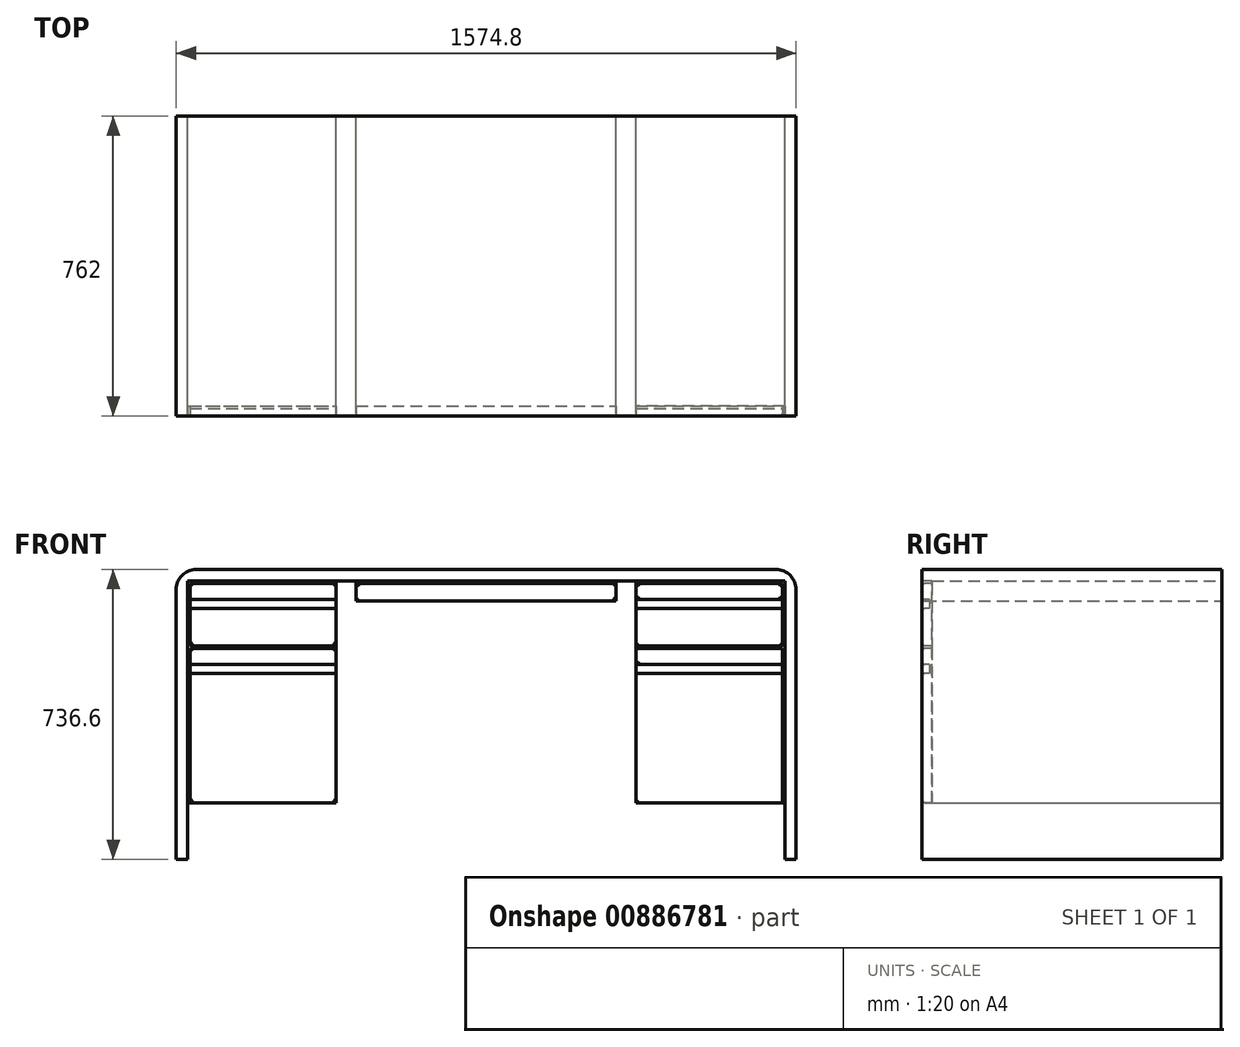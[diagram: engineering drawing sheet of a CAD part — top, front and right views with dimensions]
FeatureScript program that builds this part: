
annotation { "Feature Type Name" : "Feature", "Feature Type Description" : "" }
export const myFeature = defineFeature(function(context is Context, id is Id, definition is map)
    precondition{}
    {
        {
            var Q0;
            Q0=qCreatedBy(makeId("Front.planeOp"),FACE);
            var sketch = newSketch(context, id + "F0", { "sketchPlane" : qUnion([Q0])});
            skLineSegment(sketch, "E0.bottom", {"start": v(-787.4, 368.3) * mm, "end": v(787.4, 368.3) * mm});
            skLineSegment(sketch, "E0.top", {"start": v(-787.4, -368.3) * mm, "end": v(-758.83, -368.3) * mm});
            skLineSegment(sketch, "E0.left", {"start": v(-787.4, 368.3) * mm, "end": v(-787.4, -368.3) * mm});
            skLineSegment(sketch, "E0.right", {"start": v(787.4, 368.3) * mm, "end": v(787.4, -368.3) * mm});
            skPoint(sketch, "E0.middle", {"position": v(0, 0) * mm});
            skLineSegment(sketch, "E1", {"start": v(-758.83, -368.3) * mm, "end": v(-758.83, -224.1) * mm});
            skLineSegment(sketch, "E2", {"start": v(-758.83, -224.1) * mm, "end": v(-381, -224.1) * mm});
            skLineSegment(sketch, "E3", {"start": v(-381, -224.1) * mm, "end": v(-381, 339.73) * mm});
            skLineSegment(sketch, "E4", {"start": v(-381, 339.73) * mm, "end": v(-330.2, 339.73) * mm});
            skLineSegment(sketch, "E5", {"start": v(-330.2, 339.72) * mm, "end": v(-330.2, 288.93) * mm});
            skLineSegment(sketch, "E6", {"start": v(-330.2, 288.93) * mm, "end": v(330.2, 288.93) * mm});
            skLineSegment(sketch, "E7", {"start": v(330.2, 288.93) * mm, "end": v(330.2, 339.73) * mm});
            skLineSegment(sketch, "E8", {"start": v(330.2, 339.73) * mm, "end": v(381, 339.73) * mm});
            skLineSegment(sketch, "E9", {"start": v(381, 339.73) * mm, "end": v(381, -224.1) * mm});
            skLineSegment(sketch, "E10", {"start": v(381, -224.1) * mm, "end": v(758.83, -224.1) * mm});
            skLineSegment(sketch, "E11", {"start": v(758.83, -224.1) * mm, "end": v(758.83, -368.3) * mm});
            skLineSegment(sketch, "E12.trimOffspring", {"start": v(758.83, -368.3) * mm, "end": v(787.4, -368.3) * mm});
            skSolve(sketch);
        }
        {
            var Q0;
            Q0=makeQuery(id+"F0.imprint","IMPRINT",FACE,{"disambiguationData":[TD([[makeQuery(id+"F0.imprint","IMPRINT",EDGE,{"derivedFrom":sQuery(id+"F0.wireOp",EDGE,"E0.bottom")}),-1.0]])]});
            extrude(context, id + "F1", {"entities" : qUnion([Q0]), "endBound" : BoundingType.SYMMETRIC, "depth" : 762 * mm, "offsetDistance" : 25.4 * mm});
        }
        {
            var Q0;
            Q0=makeQuery(id+"F1.opExtrude","SWEPT_EDGE",EDGE,{"disambiguationData":[OSD([sQuery(id+"F0.wireOp",EDGE,"E0.bottom"),sQuery(id+"F0.wireOp",EDGE,"E0.right")])]});
            var Q1;
            Q1=makeQuery(id+"F1.opExtrude","SWEPT_EDGE",EDGE,{"disambiguationData":[OSD([sQuery(id+"F0.wireOp",EDGE,"E0.bottom"),sQuery(id+"F0.wireOp",EDGE,"E0.left")])]});
            fillet(context, id + "F2", {"entities" : qUnion([Q0, Q1]), "radius" : 50.8 * mm, "tangentPropagation" : true, "allowEdgeOverflow" : false});
        }
        {
            var Q0;
            Q0=makeQuery(id+"F1.opExtrude","CAP_FACE",FACE,{"disambiguationData":[OSD([sQuery(id+"F0.wireOp",EDGE,"E0.bottom"),sQuery(id+"F0.wireOp",EDGE,"E0.top"),sQuery(id+"F0.wireOp",EDGE,"E0.left"),sQuery(id+"F0.wireOp",EDGE,"E0.right"),sQuery(id+"F0.wireOp",EDGE,"E1"),sQuery(id+"F0.wireOp",EDGE,"E2"),sQuery(id+"F0.wireOp",EDGE,"E3"),sQuery(id+"F0.wireOp",EDGE,"E4"),sQuery(id+"F0.wireOp",EDGE,"E5"),sQuery(id+"F0.wireOp",EDGE,"E6"),sQuery(id+"F0.wireOp",EDGE,"E7"),sQuery(id+"F0.wireOp",EDGE,"E8"),sQuery(id+"F0.wireOp",EDGE,"E9"),sQuery(id+"F0.wireOp",EDGE,"E10"),sQuery(id+"F0.wireOp",EDGE,"E11"),sQuery(id+"F0.wireOp",EDGE,"E12.trimOffspring")])],"isStart":false});
            var sketch = newSketch(context, id + "F3", { "sketchPlane" : qUnion([Q0])});
            skLineSegment(sketch, "E13", {"start": v(-758.83, -224.1) * mm, "end": v(-758.83, 339.73) * mm});
            skLineSegment(sketch, "E14", {"start": v(-758.83, 339.73) * mm, "end": v(-381, 339.73) * mm});
            skLineSegment(sketch, "E15", {"start": v(-752.48, -224.1) * mm, "end": v(-752.48, 168.28) * mm});
            skLineSegment(sketch, "E16", {"start": v(-752.48, 333.38) * mm, "end": v(-381, 333.38) * mm});
            skLineSegment(sketch, "E17", {"start": v(-752.48, 174.63) * mm, "end": v(-381, 174.63) * mm});
            skLineSegment(sketch, "E18", {"start": v(-752.48, 168.28) * mm, "end": v(-381, 168.28) * mm});
            skLineSegment(sketch, "E19.trimOffspring", {"start": v(-752.48, 174.63) * mm, "end": v(-752.48, 333.38) * mm});
            skLineSegment(sketch, "E20", {"start": v(-330.2, 339.73) * mm, "end": v(330.2, 339.73) * mm});
            skLineSegment(sketch, "E21", {"start": v(-330.2, 333.38) * mm, "end": v(330.2, 333.38) * mm});
            skLineSegment(sketch, "E22", {"start": v(758.83, -224.1) * mm, "end": v(758.83, 339.73) * mm});
            skLineSegment(sketch, "E23", {"start": v(758.83, 339.73) * mm, "end": v(381, 339.73) * mm});
            skLineSegment(sketch, "E24", {"start": v(381, 333.38) * mm, "end": v(752.48, 333.38) * mm});
            skLineSegment(sketch, "E25", {"start": v(752.48, 333.38) * mm, "end": v(752.48, 174.63) * mm});
            skLineSegment(sketch, "E26", {"start": v(381, 174.63) * mm, "end": v(752.48, 174.63) * mm});
            skLineSegment(sketch, "E27", {"start": v(381, 168.28) * mm, "end": v(752.48, 168.28) * mm});
            skLineSegment(sketch, "E28.trimOffspring", {"start": v(752.48, 168.28) * mm, "end": v(752.48, -224.1) * mm});
            skLineSegment(sketch, "E29", {"start": v(-752.48, 292.1) * mm, "end": v(-381, 292.1) * mm});
            skLineSegment(sketch, "E30", {"start": v(-752.48, 269.87) * mm, "end": v(-381, 269.87) * mm});
            skLineSegment(sketch, "E31", {"start": v(-752.48, 127) * mm, "end": v(-381, 127) * mm});
            skLineSegment(sketch, "E32", {"start": v(-752.48, 104.77) * mm, "end": v(-381, 104.77) * mm});
            skLineSegment(sketch, "E33", {"start": v(381, 292.1) * mm, "end": v(752.48, 292.1) * mm});
            skLineSegment(sketch, "E34", {"start": v(381, 269.87) * mm, "end": v(752.48, 269.87) * mm});
            skLineSegment(sketch, "E35", {"start": v(381, 127) * mm, "end": v(752.48, 127) * mm});
            skLineSegment(sketch, "E36", {"start": v(381, 104.77) * mm, "end": v(752.48, 104.77) * mm});
            skSolve(sketch);
        }
        {
            var Q0;
            {var subQ8=sQuery(id+"F3.wireOp",EDGE,"E13");Q0=makeQuery(id+"F3.imprint","IMPRINT",FACE,{"disambiguationData":[TD([[makeQuery(id+"F3.imprint","IMPRINT",EDGE,{"derivedFrom":subQ8}),-1.0]])]});}
            var Q1;
            {var subQ0=sQuery(id+"F3.wireOp",EDGE,"E20");Q1=makeQuery(id+"F3.imprint","IMPRINT",FACE,{"disambiguationData":[TD([[makeQuery(id+"F3.imprint","IMPRINT",EDGE,{"derivedFrom":subQ0}),-1.0]])]});}
            var Q2;
            {var subQ4=sQuery(id+"F3.wireOp",EDGE,"E22");Q2=makeQuery(id+"F3.imprint","IMPRINT",FACE,{"disambiguationData":[TD([[makeQuery(id+"F3.imprint","IMPRINT",EDGE,{"derivedFrom":subQ4}),1.0]])]});}
            extrude(context, id + "F4", {"entities" : qUnion([Q0, Q1, Q2]), "operationType" : NewBodyOperationType.REMOVE, "oppositeDirection" : true, "depth" : 25.4 * mm, "offsetDistance" : 25.4 * mm});
        }
        {
            var Q0;
            {var subQ0=sQuery(id+"F3.wireOp",EDGE,"E31");Q0=makeQuery(id+"F3.imprint","IMPRINT",FACE,{"disambiguationData":[TD([[makeQuery(id+"F3.imprint","IMPRINT",EDGE,{"derivedFrom":subQ0}),-1.0]])]});}
            var Q1;
            {var subQ0=sQuery(id+"F3.wireOp",EDGE,"E29");Q1=makeQuery(id+"F3.imprint","IMPRINT",FACE,{"disambiguationData":[TD([[makeQuery(id+"F3.imprint","IMPRINT",EDGE,{"derivedFrom":subQ0}),-1.0]])]});}
            var Q2;
            {var subQ0=sQuery(id+"F3.wireOp",EDGE,"E33");Q2=makeQuery(id+"F3.imprint","IMPRINT",FACE,{"disambiguationData":[TD([[makeQuery(id+"F3.imprint","IMPRINT",EDGE,{"derivedFrom":subQ0}),-1.0]])]});}
            var Q3;
            {var subQ0=sQuery(id+"F3.wireOp",EDGE,"E35");Q3=makeQuery(id+"F3.imprint","IMPRINT",FACE,{"disambiguationData":[TD([[makeQuery(id+"F3.imprint","IMPRINT",EDGE,{"derivedFrom":subQ0}),-1.0]])]});}
            extrude(context, id + "F5", {"entities" : qUnion([Q0, Q1, Q2, Q3]), "operationType" : NewBodyOperationType.REMOVE, "oppositeDirection" : true, "depth" : 19.05 * mm, "offsetDistance" : 25.4 * mm});
        }
        {
            var Q0;
            Q0=makeQuery(id+"F1.opExtrude","CAP_EDGE",EDGE,{"disambiguationData":[OSD([sQuery(id+"F0.wireOp",EDGE,"E2")])],"isStart":false});
            var Q1;
            {var subQ0=sQuery(id+"F0.wireOp",EDGE,"E3");var subQ1=sQuery(id+"F0.wireOp",EDGE,"E2");var subQ3=makeQuery(id+"F1.opExtrude","SWEPT_FACE",FACE,{"disambiguationData":[OSD([subQ1])]});Q1=makeQuery(id+"F5.boolean.opBoolean","SPLIT",EDGE,{"disambiguationData":[TD([subQ3])],"derivedFrom":makeQuery(id+"F4.boolean.opBoolean","SPLIT",EDGE,{"disambiguationData":[TD([subQ3])],"derivedFrom":makeQuery(id+"F1.opExtrude","CAP_EDGE",EDGE,{"disambiguationData":[OSD([subQ0])],"isStart":false})})});}
            var Q2;
            {var subQ0=sQuery(id+"F0.wireOp",EDGE,"E3");var subQ1=sQuery(id+"F0.wireOp",EDGE,"E2");var subQ3=makeQuery(id+"F4.opExtrude","SWEPT_FACE",FACE,{"disambiguationData":[OSD([sQuery(id+"F3.wireOp",EDGE,"E18")])]});Q2=makeQuery(id+"F5.boolean.opBoolean","SPLIT",EDGE,{"disambiguationData":[TD([makeQuery(id+"F4.boolean.opBoolean","COPY",FACE,{"derivedFrom":subQ3})])],"derivedFrom":makeQuery(id+"F4.boolean.opBoolean","SPLIT",EDGE,{"disambiguationData":[TD([makeQuery(id+"F1.opExtrude","SWEPT_FACE",FACE,{"disambiguationData":[OSD([subQ1])]})])],"derivedFrom":makeQuery(id+"F1.opExtrude","CAP_EDGE",EDGE,{"disambiguationData":[OSD([subQ0])],"isStart":false})})});}
            var Q3;
            {var subQ0=sQuery(id+"F0.wireOp",EDGE,"E3");var subQ3=makeQuery(id+"F4.opExtrude","SWEPT_FACE",FACE,{"disambiguationData":[OSD([sQuery(id+"F3.wireOp",EDGE,"E17")])]});Q3=makeQuery(id+"F5.boolean.opBoolean","SPLIT",EDGE,{"disambiguationData":[TD([makeQuery(id+"F4.boolean.opBoolean","COPY",FACE,{"derivedFrom":subQ3})])],"derivedFrom":makeQuery(id+"F4.boolean.opBoolean","SPLIT",EDGE,{"disambiguationData":[TD([makeQuery(id+"F4.opExtrude","SWEPT_FACE",FACE,{"disambiguationData":[OSD([sQuery(id+"F3.wireOp",EDGE,"E16")])]})])],"derivedFrom":makeQuery(id+"F1.opExtrude","CAP_EDGE",EDGE,{"disambiguationData":[OSD([subQ0])],"isStart":false})})});}
            var Q4;
            Q4=makeQuery(id+"F4.boolean.opBoolean","COPY",EDGE,{"derivedFrom":makeQuery(id+"F4.opExtrude","CAP_EDGE",EDGE,{"disambiguationData":[OSD([sQuery(id+"F3.wireOp",EDGE,"E18")])],"isStart":true})});
            var Q5;
            Q5=makeQuery(id+"F4.boolean.opBoolean","COPY",EDGE,{"derivedFrom":makeQuery(id+"F4.opExtrude","CAP_EDGE",EDGE,{"disambiguationData":[OSD([sQuery(id+"F3.wireOp",EDGE,"E17")])],"isStart":true})});
            var Q6;
            {var subQ0=sQuery(id+"F0.wireOp",EDGE,"E3");var subQ3=makeQuery(id+"F4.opExtrude","SWEPT_FACE",FACE,{"disambiguationData":[OSD([sQuery(id+"F3.wireOp",EDGE,"E16")])]});Q6=makeQuery(id+"F5.boolean.opBoolean","SPLIT",EDGE,{"disambiguationData":[TD([makeQuery(id+"F4.boolean.opBoolean","COPY",FACE,{"derivedFrom":subQ3})])],"derivedFrom":makeQuery(id+"F4.boolean.opBoolean","SPLIT",EDGE,{"disambiguationData":[TD([subQ3])],"derivedFrom":makeQuery(id+"F1.opExtrude","CAP_EDGE",EDGE,{"disambiguationData":[OSD([subQ0])],"isStart":false})})});}
            var Q7;
            Q7=makeQuery(id+"F4.boolean.opBoolean","COPY",EDGE,{"derivedFrom":makeQuery(id+"F4.opExtrude","CAP_EDGE",EDGE,{"disambiguationData":[OSD([sQuery(id+"F3.wireOp",EDGE,"E16")])],"isStart":true})});
            var Q8;
            {var subQ0=sQuery(id+"F3.wireOp",EDGE,"E19.trimOffspring");Q8=makeQuery(id+"F5.boolean.opBoolean","SPLIT",EDGE,{"disambiguationData":[TD([makeQuery(id+"F4.boolean.opBoolean","COPY",FACE,{"derivedFrom":makeQuery(id+"F4.opExtrude","SWEPT_FACE",FACE,{"disambiguationData":[OSD([sQuery(id+"F3.wireOp",EDGE,"E16")])]})})])],"derivedFrom":makeQuery(id+"F4.boolean.opBoolean","COPY",EDGE,{"derivedFrom":makeQuery(id+"F4.opExtrude","CAP_EDGE",EDGE,{"disambiguationData":[OSD([subQ0])],"isStart":true})})});}
            var Q9;
            {var subQ0=sQuery(id+"F3.wireOp",EDGE,"E19.trimOffspring");Q9=makeQuery(id+"F5.boolean.opBoolean","SPLIT",EDGE,{"disambiguationData":[TD([makeQuery(id+"F4.boolean.opBoolean","COPY",FACE,{"derivedFrom":makeQuery(id+"F4.opExtrude","SWEPT_FACE",FACE,{"disambiguationData":[OSD([sQuery(id+"F3.wireOp",EDGE,"E17")])]})})])],"derivedFrom":makeQuery(id+"F4.boolean.opBoolean","COPY",EDGE,{"derivedFrom":makeQuery(id+"F4.opExtrude","CAP_EDGE",EDGE,{"disambiguationData":[OSD([subQ0])],"isStart":true})})});}
            var Q10;
            {var subQ0=sQuery(id+"F3.wireOp",EDGE,"E15");Q10=makeQuery(id+"F5.boolean.opBoolean","SPLIT",EDGE,{"disambiguationData":[TD([makeQuery(id+"F4.boolean.opBoolean","COPY",FACE,{"derivedFrom":makeQuery(id+"F4.opExtrude","SWEPT_FACE",FACE,{"disambiguationData":[OSD([sQuery(id+"F3.wireOp",EDGE,"E18")])]})})])],"derivedFrom":makeQuery(id+"F4.boolean.opBoolean","COPY",EDGE,{"derivedFrom":makeQuery(id+"F4.opExtrude","CAP_EDGE",EDGE,{"disambiguationData":[OSD([subQ0])],"isStart":true})})});}
            var Q11;
            {var subQ0=sQuery(id+"F0.wireOp",EDGE,"E2");var subQ1=sQuery(id+"F3.wireOp",EDGE,"E15");Q11=makeQuery(id+"F5.boolean.opBoolean","SPLIT",EDGE,{"disambiguationData":[TD([makeQuery(id+"F1.opExtrude","SWEPT_FACE",FACE,{"disambiguationData":[OSD([subQ0])]})])],"derivedFrom":makeQuery(id+"F4.boolean.opBoolean","COPY",EDGE,{"derivedFrom":makeQuery(id+"F4.opExtrude","CAP_EDGE",EDGE,{"disambiguationData":[OSD([subQ1])],"isStart":true})})});}
            var Q12;
            Q12=makeQuery(id+"F1.opExtrude","CAP_EDGE",EDGE,{"disambiguationData":[OSD([sQuery(id+"F0.wireOp",EDGE,"E5")])],"isStart":false});
            var Q13;
            Q13=makeQuery(id+"F1.opExtrude","CAP_EDGE",EDGE,{"disambiguationData":[OSD([sQuery(id+"F0.wireOp",EDGE,"E6")])],"isStart":false});
            var Q14;
            Q14=makeQuery(id+"F4.boolean.opBoolean","COPY",EDGE,{"derivedFrom":makeQuery(id+"F4.opExtrude","CAP_EDGE",EDGE,{"disambiguationData":[OSD([sQuery(id+"F3.wireOp",EDGE,"E21")])],"isStart":true})});
            var Q15;
            Q15=makeQuery(id+"F1.opExtrude","CAP_EDGE",EDGE,{"disambiguationData":[OSD([sQuery(id+"F0.wireOp",EDGE,"E7")])],"isStart":false});
            var Q16;
            Q16=makeQuery(id+"F4.boolean.opBoolean","COPY",EDGE,{"derivedFrom":makeQuery(id+"F4.opExtrude","CAP_EDGE",EDGE,{"disambiguationData":[OSD([sQuery(id+"F3.wireOp",EDGE,"E24")])],"isStart":true})});
            var Q17;
            {var subQ0=sQuery(id+"F0.wireOp",EDGE,"E9");var subQ2=makeQuery(id+"F4.opExtrude","SWEPT_FACE",FACE,{"disambiguationData":[OSD([sQuery(id+"F3.wireOp",EDGE,"E24")])]});Q17=makeQuery(id+"F5.boolean.opBoolean","SPLIT",EDGE,{"disambiguationData":[TD([makeQuery(id+"F4.boolean.opBoolean","COPY",FACE,{"derivedFrom":subQ2})])],"derivedFrom":makeQuery(id+"F4.boolean.opBoolean","SPLIT",EDGE,{"disambiguationData":[TD([subQ2])],"derivedFrom":makeQuery(id+"F1.opExtrude","CAP_EDGE",EDGE,{"disambiguationData":[OSD([subQ0])],"isStart":false})})});}
            var Q18;
            Q18=makeQuery(id+"F5.boolean.opBoolean","COPY",EDGE,{"derivedFrom":makeQuery(id+"F5.opExtrude","CAP_EDGE",EDGE,{"disambiguationData":[OSD([sQuery(id+"F3.wireOp",EDGE,"E33")])],"isStart":true})});
            var Q19;
            {var subQ0=sQuery(id+"F3.wireOp",EDGE,"E25");Q19=makeQuery(id+"F5.boolean.opBoolean","SPLIT",EDGE,{"disambiguationData":[TD([makeQuery(id+"F4.boolean.opBoolean","COPY",FACE,{"derivedFrom":makeQuery(id+"F4.opExtrude","SWEPT_FACE",FACE,{"disambiguationData":[OSD([sQuery(id+"F3.wireOp",EDGE,"E24")])]})})])],"derivedFrom":makeQuery(id+"F4.boolean.opBoolean","COPY",EDGE,{"derivedFrom":makeQuery(id+"F4.opExtrude","CAP_EDGE",EDGE,{"disambiguationData":[OSD([subQ0])],"isStart":true})})});}
            var Q20;
            {var subQ0=sQuery(id+"F0.wireOp",EDGE,"E9");var subQ3=makeQuery(id+"F4.opExtrude","SWEPT_FACE",FACE,{"disambiguationData":[OSD([sQuery(id+"F3.wireOp",EDGE,"E26")])]});Q20=makeQuery(id+"F5.boolean.opBoolean","SPLIT",EDGE,{"disambiguationData":[TD([makeQuery(id+"F4.boolean.opBoolean","COPY",FACE,{"derivedFrom":subQ3})])],"derivedFrom":makeQuery(id+"F4.boolean.opBoolean","SPLIT",EDGE,{"disambiguationData":[TD([makeQuery(id+"F4.opExtrude","SWEPT_FACE",FACE,{"disambiguationData":[OSD([sQuery(id+"F3.wireOp",EDGE,"E24")])]})])],"derivedFrom":makeQuery(id+"F1.opExtrude","CAP_EDGE",EDGE,{"disambiguationData":[OSD([subQ0])],"isStart":false})})});}
            var Q21;
            Q21=makeQuery(id+"F4.boolean.opBoolean","COPY",EDGE,{"derivedFrom":makeQuery(id+"F4.opExtrude","CAP_EDGE",EDGE,{"disambiguationData":[OSD([sQuery(id+"F3.wireOp",EDGE,"E26")])],"isStart":true})});
            var Q22;
            {var subQ0=sQuery(id+"F3.wireOp",EDGE,"E25");Q22=makeQuery(id+"F5.boolean.opBoolean","SPLIT",EDGE,{"disambiguationData":[TD([makeQuery(id+"F4.boolean.opBoolean","COPY",FACE,{"derivedFrom":makeQuery(id+"F4.opExtrude","SWEPT_FACE",FACE,{"disambiguationData":[OSD([sQuery(id+"F3.wireOp",EDGE,"E26")])]})})])],"derivedFrom":makeQuery(id+"F4.boolean.opBoolean","COPY",EDGE,{"derivedFrom":makeQuery(id+"F4.opExtrude","CAP_EDGE",EDGE,{"disambiguationData":[OSD([subQ0])],"isStart":true})})});}
            var Q23;
            Q23=makeQuery(id+"F4.boolean.opBoolean","COPY",EDGE,{"derivedFrom":makeQuery(id+"F4.opExtrude","CAP_EDGE",EDGE,{"disambiguationData":[OSD([sQuery(id+"F3.wireOp",EDGE,"E27")])],"isStart":true})});
            var Q24;
            {var subQ0=sQuery(id+"F0.wireOp",EDGE,"E10");var subQ1=sQuery(id+"F0.wireOp",EDGE,"E9");var subQ4=makeQuery(id+"F4.opExtrude","SWEPT_FACE",FACE,{"disambiguationData":[OSD([sQuery(id+"F3.wireOp",EDGE,"E27")])]});Q24=makeQuery(id+"F5.boolean.opBoolean","SPLIT",EDGE,{"disambiguationData":[TD([makeQuery(id+"F4.boolean.opBoolean","COPY",FACE,{"derivedFrom":subQ4})])],"derivedFrom":makeQuery(id+"F4.boolean.opBoolean","SPLIT",EDGE,{"disambiguationData":[TD([makeQuery(id+"F1.opExtrude","SWEPT_FACE",FACE,{"disambiguationData":[OSD([subQ0])]})])],"derivedFrom":makeQuery(id+"F1.opExtrude","CAP_EDGE",EDGE,{"disambiguationData":[OSD([subQ1])],"isStart":false})})});}
            var Q25;
            Q25=makeQuery(id+"F5.boolean.opBoolean","COPY",EDGE,{"derivedFrom":makeQuery(id+"F5.opExtrude","CAP_EDGE",EDGE,{"disambiguationData":[OSD([sQuery(id+"F3.wireOp",EDGE,"E35")])],"isStart":true})});
            var Q26;
            {var subQ0=sQuery(id+"F3.wireOp",EDGE,"E28.trimOffspring");Q26=makeQuery(id+"F5.boolean.opBoolean","SPLIT",EDGE,{"disambiguationData":[TD([makeQuery(id+"F4.boolean.opBoolean","COPY",FACE,{"derivedFrom":makeQuery(id+"F4.opExtrude","SWEPT_FACE",FACE,{"disambiguationData":[OSD([sQuery(id+"F3.wireOp",EDGE,"E27")])]})})])],"derivedFrom":makeQuery(id+"F4.boolean.opBoolean","COPY",EDGE,{"derivedFrom":makeQuery(id+"F4.opExtrude","CAP_EDGE",EDGE,{"disambiguationData":[OSD([subQ0])],"isStart":true})})});}
            var Q27;
            {var subQ0=sQuery(id+"F0.wireOp",EDGE,"E10");var subQ1=sQuery(id+"F0.wireOp",EDGE,"E9");var subQ4=makeQuery(id+"F1.opExtrude","SWEPT_FACE",FACE,{"disambiguationData":[OSD([subQ0])]});Q27=makeQuery(id+"F5.boolean.opBoolean","SPLIT",EDGE,{"disambiguationData":[TD([subQ4])],"derivedFrom":makeQuery(id+"F4.boolean.opBoolean","SPLIT",EDGE,{"disambiguationData":[TD([subQ4])],"derivedFrom":makeQuery(id+"F1.opExtrude","CAP_EDGE",EDGE,{"disambiguationData":[OSD([subQ1])],"isStart":false})})});}
            var Q28;
            {var subQ0=sQuery(id+"F0.wireOp",EDGE,"E10");var subQ1=sQuery(id+"F3.wireOp",EDGE,"E28.trimOffspring");Q28=makeQuery(id+"F5.boolean.opBoolean","SPLIT",EDGE,{"disambiguationData":[TD([makeQuery(id+"F1.opExtrude","SWEPT_FACE",FACE,{"disambiguationData":[OSD([subQ0])]})])],"derivedFrom":makeQuery(id+"F4.boolean.opBoolean","COPY",EDGE,{"derivedFrom":makeQuery(id+"F4.opExtrude","CAP_EDGE",EDGE,{"disambiguationData":[OSD([subQ1])],"isStart":true})})});}
            var Q29;
            Q29=makeQuery(id+"F1.opExtrude","CAP_EDGE",EDGE,{"disambiguationData":[OSD([sQuery(id+"F0.wireOp",EDGE,"E10")])],"isStart":false});
            fillet(context, id + "F6", {"entities" : qUnion([Q0, Q1, Q2, Q3, Q4, Q5, Q6, Q7, Q8, Q9, Q10, Q11, Q12, Q13, Q14, Q15, Q16, Q17, Q18, Q19, Q20, Q21, Q22, Q23, Q24, Q25, Q26, Q27, Q28, Q29]), "radius" : 6.35 * mm, "tangentPropagation" : true, "allowEdgeOverflow" : false});
        }
    });
